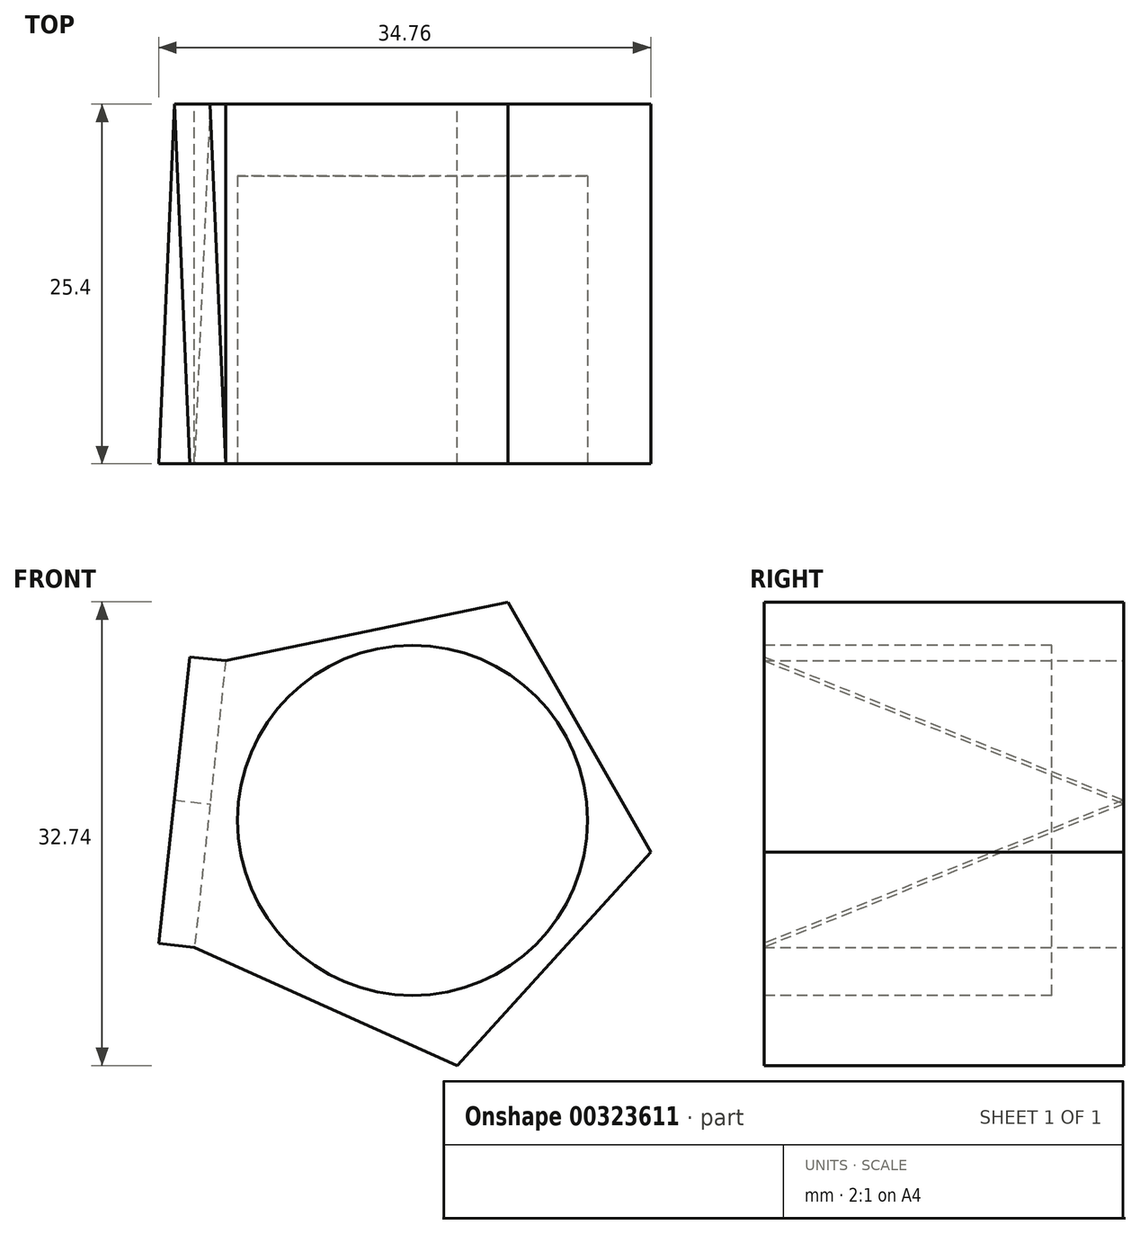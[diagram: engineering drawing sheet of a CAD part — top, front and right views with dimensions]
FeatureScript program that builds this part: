
annotation { "Feature Type Name" : "Feature", "Feature Type Description" : "" }
export const myFeature = defineFeature(function(context is Context, id is Id, definition is map)
    precondition{}
    {
        {
            var Q0;
            Q0=qCreatedBy(makeId("Front.planeOp"),FACE);
            var sketch = newSketch(context, id + "F0", { "sketchPlane" : qUnion([Q0])});
            skCircle(sketch, "E0.cCircle", {"center": v(18.68, 23.25) * mm, "radius": 14 * mm, "construction": true});
            skLineSegment(sketch, "E0.0", {"start": v(35.9, 21.37) * mm, "end": v(22.21, 6.3) * mm});
            skLineSegment(sketch, "E0.1", {"start": v(22.21, 6.3) * mm, "end": v(3.65, 14.65) * mm});
            skLineSegment(sketch, "E0.2", {"start": v(3.65, 14.65) * mm, "end": v(5.86, 34.89) * mm});
            skLineSegment(sketch, "E0.3", {"start": v(5.86, 34.89) * mm, "end": v(25.79, 39.04) * mm});
            skLineSegment(sketch, "E0.4", {"start": v(25.79, 39.04) * mm, "end": v(35.9, 21.37) * mm});
            skPoint(sketch, "E0.0.midPoint", {"position": v(29.05, 13.83) * mm});
            skSolve(sketch);
        }
        {
            var Q0;
            Q0 = qSketchRegion(id + "F0", true);
            extrude(context, id + "F1", {"entities" : qUnion([Q0]), "depth" : 25.4 * mm});
        }
        {
            var Q0;
            Q0=makeQuery(id+"F1.opExtrude","CAP_FACE",FACE,{"disambiguationData":[OSD([sQuery(id+"F0.wireOp",EDGE,"E0.0"),sQuery(id+"F0.wireOp",EDGE,"E0.1"),sQuery(id+"F0.wireOp",EDGE,"E0.2"),sQuery(id+"F0.wireOp",EDGE,"E0.3"),sQuery(id+"F0.wireOp",EDGE,"E0.4")])],"isStart":false});
            var sketch = newSketch(context, id + "F2", { "sketchPlane" : qUnion([Q0])});
            skCircle(sketch, "E1", {"center": v(19.06, 23.62) * mm, "radius": 12.37 * mm});
            skSolve(sketch);
        }
        {
            var Q0;
            Q0=makeQuery(id+"F2.imprint","IMPRINT",FACE,{"disambiguationData":[TD([[makeQuery(id+"F2.imprint","IMPRINT",EDGE,{"derivedFrom":sQuery(id+"F2.wireOp",EDGE,"E1")}),1.0]])]});
            var Q1;
            Q1=sQuery(id+"F2.wireOp",EDGE,"E1");
            extrude(context, id + "F3", {"entities" : qUnion([Q0]), "operationType" : NewBodyOperationType.REMOVE, "surfaceEntities" : qUnion([Q1]), "oppositeDirection" : true, "depth" : 20.32 * mm});
        }
        {
            var Q0;
            Q0=makeQuery(id+"F1.opExtrude","SWEPT_FACE",FACE,{"disambiguationData":[OSD([sQuery(id+"F0.wireOp",EDGE,"E0.2")])]});
            var sketch = newSketch(context, id + "F4", { "sketchPlane" : qUnion([Q0])});
            skLineSegment(sketch, "E2", {"start": v(25.4, 35.32) * mm, "end": v(0, 25.14) * mm});
            skLineSegment(sketch, "E3", {"start": v(0, 25.14) * mm, "end": v(25.4, 14.96) * mm});
            skSolve(sketch);
        }
        {
            var Q0;
            Q0=makeQuery(id+"F4.imprint","IMPRINT",FACE,{"disambiguationData":[TD([[makeQuery(id+"F4.imprint","IMPRINT",EDGE,{"derivedFrom":sQuery(id+"F4.wireOp",EDGE,"E2")}),1.0]])]});
            extrude(context, id + "F5", {"entities" : qUnion([Q0]), "operationType" : NewBodyOperationType.ADD, "depth" : 2.54 * mm});
        }
    });
